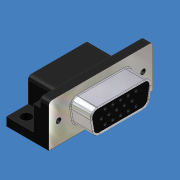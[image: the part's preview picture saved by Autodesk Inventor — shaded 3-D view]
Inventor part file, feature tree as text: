
AUTODESK INVENTOR PART (.ipt)
format: ipt  version: unknown  size: 355,840 bytes
history: native  units: mm (DEFAULTED — no unit token found)
features: sketch x7, extrude x5, fillet x2, hole x2, pattern_linear x1
ambient origin geometry x8: Origin, YZ Plane, XZ Plane, XY Plane, X Axis, Y Axis, Z Axis, Center Point
feature tree (17):
  extrude  "Extrusion1"  Depth=12.5mm
  extrude  "Extrusion4"  Depth=17.453293mm
  extrude  "Extrusion2"  Depth=16.92mm
  fillet  "Fillet1"  Radius=0.5mm
  hole  "Hole1"  [1 undecoded]
  extrude  "Extrusion3"  Depth=1.98mm
  pattern_linear  "Rectangular Pattern1"  Spacing1=0.5mm  [1 undecoded]
  fillet  "Fillet3"  Radius=0.76mm
  hole  "Hole2"  [1 undecoded]
  extrude  "Extrusion5"  Depth=2.75mm
  sketch  "Sketch1"  dims[d4=12.5mm d5=12.5mm]
  sketch  "Sketch2"  dims[d6=30.8mm d7=0.0mm d9=17.453293mm]
  sketch  "Sketch3"  dims[d11=1.5mm d12=16.92mm d13=0.5mm]
  sketch  "Sketch4"  dims[d14=6.1mm d15=0.0mm d16=0.25mm]
  sketch  "Sketch6"  dims[d17=25.0mm]
  sketch  "Sketch7"  dims[d18=1.5mm d19=6.0mm d20=4.0mm d21=2.0mm d22=14.3117mm d23=8.0mm d24=20.594885mm d27=1.98mm]
  sketch  "Sketch8"  dims[d28=4.56mm d29=0.5mm d30=0.0mm d31=0.76mm d33=100.0mm d35=1.14mm d36=30.0mm d38=1.98mm d40=2.75mm d41=2.5mm d42=18.0mm d43=2.0mm d44=7.25mm d45=0.0mm d46=1.0mm d47=9.525mm d48=25.0mm d49=3.0mm d50=6.0mm d51=4.0mm d52=2.0mm d53=14.3117mm d54=8.0mm d55=20.594885mm d56=7.3mm d57=5.85mm d58=0.0mm]
note: 3 required parameter values undecoded (feature->parameter linkage not recoverable at this tier; creation-order binding heuristic only, values carry confidence <= 0.55)
